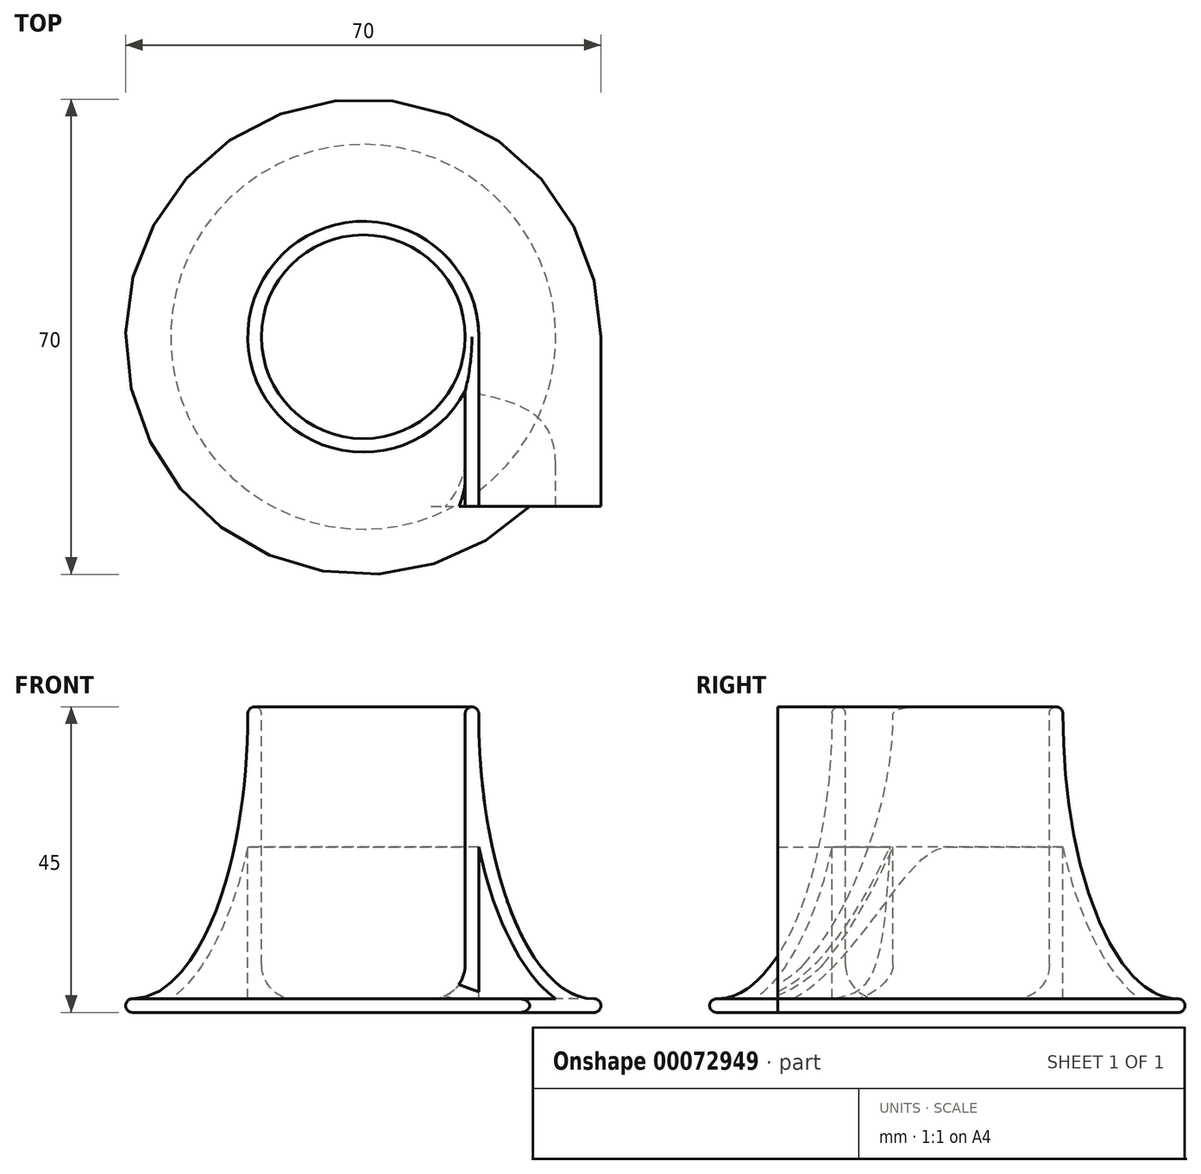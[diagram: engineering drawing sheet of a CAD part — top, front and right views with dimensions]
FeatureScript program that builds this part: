
annotation { "Feature Type Name" : "Feature", "Feature Type Description" : "" }
export const myFeature = defineFeature(function(context is Context, id is Id, definition is map)
    precondition{}
    {
        {
            var Q0;
            Q0=qCreatedBy(makeId("Front.planeOp"),FACE);
            var sketch = newSketch(context, id + "F0", { "sketchPlane" : qUnion([Q0])});
            skLineSegment(sketch, "E0", {"start": v(0, 0) * mm, "end": v(34, 0) * mm});
            skLineSegment(sketch, "E1", {"start": v(0, 2) * mm, "end": v(0, 0) * mm});
            skLineSegment(sketch, "E2", {"start": v(20, 22) * mm, "end": v(20, 13.54) * mm, "construction": true});
            skEllipticalArc(sketch, "E3.0.MirrorC", {});
            skArc(sketch, "E4", {"start": v(17, 44) * mm, "mid": v(16, 45) * mm, "end": v(15, 44) * mm});
            skLineSegment(sketch, "E5", {"start": v(34, 2) * mm, "end": v(34, 0) * mm, "construction": true});
            skArc(sketch, "E6", {"start": v(34, 0) * mm, "mid": v(35, 1) * mm, "end": v(34, 2) * mm});
            skLineSegment(sketch, "E7", {"start": v(15, 44) * mm, "end": v(17, 44) * mm, "construction": true});
            skLineSegment(sketch, "E8", {"start": v(15, 44) * mm, "end": v(15, 7) * mm});
            skLineSegment(sketch, "E9", {"start": v(10, 2) * mm, "end": v(0, 2) * mm});
            skPoint(sketch, "E10.visualSharp", {"position": v(15, 2) * mm});
            skArc(sketch, "E10.filletArc", {"start": v(10, 2) * mm, "mid": v(13.54, 3.46) * mm, "end": v(15, 7) * mm});
            skLineSegment(sketch, "E11", {"start": v(17, 24.35) * mm, "end": v(17, 2) * mm});
            skLineSegment(sketch, "E12", {"start": v(17, 2) * mm, "end": v(28.34, 2) * mm});
            skEllipticalArc(sketch, "E13", {});
            const initialGuessF0  = {"E3.0.MirrorC": [0.034, 0.044, 0, -1, 0.042, 0.017, 4.71238898038469, 0], "E13": [0.034, 0.044, 0, -1, 0.044, 0.019, 5.175343708325145, 5.9805200332251545]};
            skSetInitialGuess(sketch, initialGuessF0);
            skSolve(sketch);
        }
        {
            var Q0;
            Q0=qSketchRegion(id+"F0",true);
            var Q1;
            Q1=sQuery(id+"F0.wireOp",EDGE,"E1");
            revolve(context, id + "F1", {"entities" : qUnion([Q0]), "axis" : qUnion([Q1]), "revolveType" : RevolveType.FULL});
        }
        {
            var Q0;
            Q0 = qSketchRegion(id + "F0", true);
            extrude(context, id + "F2", {"entities" : qUnion([Q0]), "operationType" : NewBodyOperationType.ADD, "depth" : 25 * mm});
        }
    });
